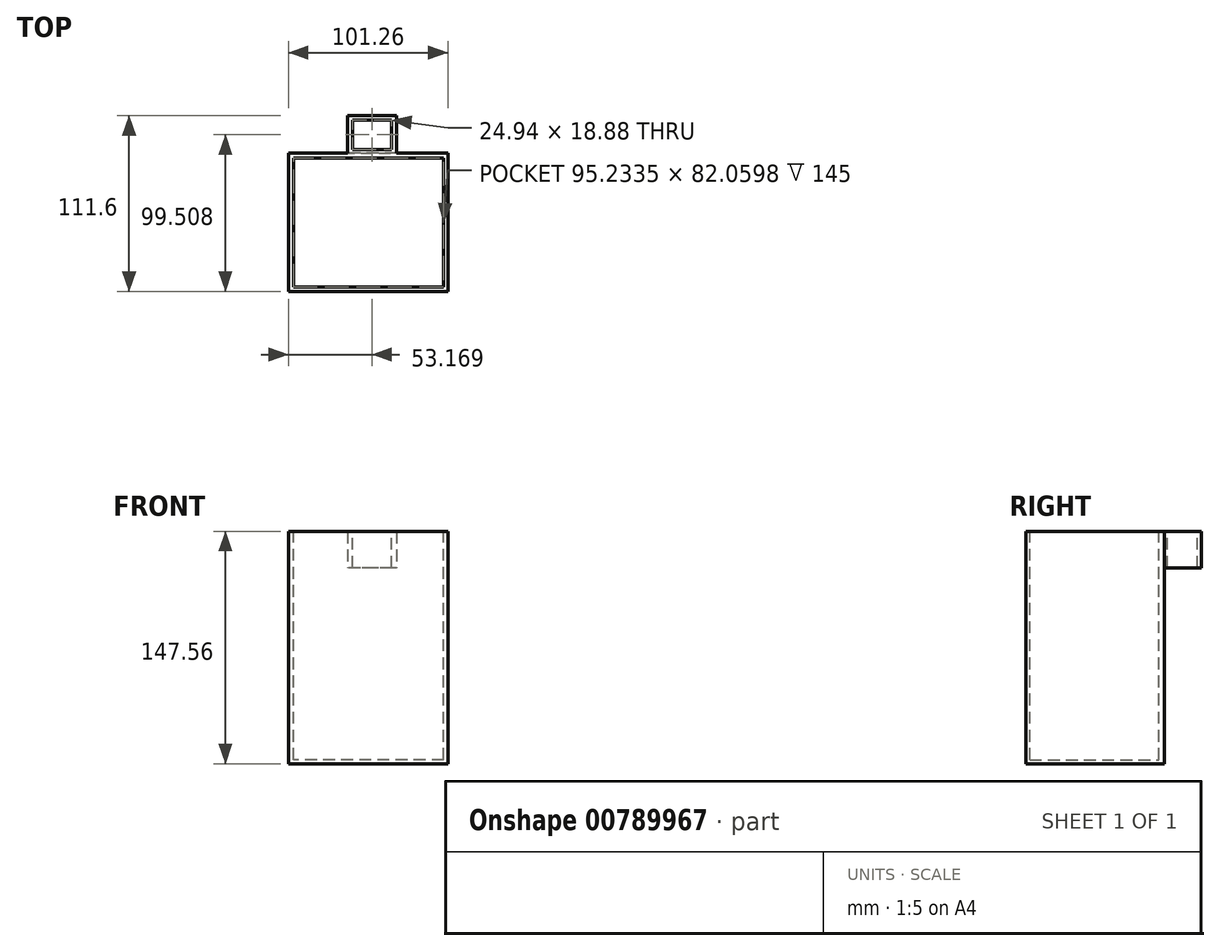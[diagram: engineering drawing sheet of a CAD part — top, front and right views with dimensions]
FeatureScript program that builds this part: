
annotation { "Feature Type Name" : "Feature", "Feature Type Description" : "" }
export const myFeature = defineFeature(function(context is Context, id is Id, definition is map)
    precondition{}
    {
        {
            var Q0;
            Q0=qCreatedBy(makeId("Front.planeOp"),FACE);
            var sketch = newSketch(context, id + "F0", { "sketchPlane" : qUnion([Q0])});
            skLineSegment(sketch, "E0.bottom", {"start": v(-75.3, 74) * mm, "end": v(25.97, 74) * mm});
            skLineSegment(sketch, "E0.top", {"start": v(-75.3, -73.57) * mm, "end": v(25.97, -73.57) * mm});
            skLineSegment(sketch, "E0.left", {"start": v(-75.3, 74) * mm, "end": v(-75.3, -73.57) * mm});
            skLineSegment(sketch, "E0.right", {"start": v(25.97, 74) * mm, "end": v(25.97, -73.57) * mm});
            skSolve(sketch);
        }
        {
            var Q0;
            Q0=makeQuery(id+"F0.imprint","IMPRINT",FACE,{"disambiguationData":[TD([[makeQuery(id+"F0.imprint","IMPRINT",EDGE,{"derivedFrom":sQuery(id+"F0.wireOp",EDGE,"E0.bottom")}),-1.0]])]});
            extrude(context, id + "F1", {"entities" : qUnion([Q0]), "depth" : 88 * mm, "offsetDistance" : 25 * mm});
        }
        {
            var Q0;
            Q0=makeQuery(id+"F1.opExtrude","SWEPT_FACE",FACE,{"disambiguationData":[OSD([sQuery(id+"F0.wireOp",EDGE,"E0.bottom")])]});
            var sketch = newSketch(context, id + "F2", { "sketchPlane" : qUnion([Q0])});
            skLineSegment(sketch, "E1.bottom", {"start": v(23.28, -85.37) * mm, "end": v(-71.96, -85.37) * mm});
            skLineSegment(sketch, "E1.top", {"start": v(23.28, -3.3) * mm, "end": v(-71.96, -3.3) * mm});
            skLineSegment(sketch, "E1.left", {"start": v(23.28, -85.37) * mm, "end": v(23.28, -3.3) * mm});
            skLineSegment(sketch, "E1.right", {"start": v(-71.96, -85.37) * mm, "end": v(-71.96, -3.3) * mm});
            skSolve(sketch);
        }
        {
            var Q0;
            Q0=makeQuery(id+"F2.imprint","IMPRINT",FACE,{"disambiguationData":[TD([[makeQuery(id+"F2.imprint","IMPRINT",EDGE,{"derivedFrom":sQuery(id+"F2.wireOp",EDGE,"E1.bottom")}),-1.0]])]});
            extrude(context, id + "F3", {"entities" : qUnion([Q0]), "operationType" : NewBodyOperationType.REMOVE, "oppositeDirection" : true, "depth" : 145 * mm, "offsetDistance" : 25 * mm});
        }
        {
            var Q0;
            Q0=makeQuery(id+"F1.opExtrude","CAP_FACE",FACE,{"disambiguationData":[OSD([sQuery(id+"F0.wireOp",EDGE,"E0.bottom"),sQuery(id+"F0.wireOp",EDGE,"E0.top"),sQuery(id+"F0.wireOp",EDGE,"E0.left"),sQuery(id+"F0.wireOp",EDGE,"E0.right")])],"isStart":true});
            var sketch = newSketch(context, id + "F4", { "sketchPlane" : qUnion([Q0])});
            skLineSegment(sketch, "E2.bottom", {"start": v(6.55, 74) * mm, "end": v(37.64, 74) * mm});
            skLineSegment(sketch, "E2.top", {"start": v(6.55, 50.94) * mm, "end": v(37.64, 50.94) * mm});
            skLineSegment(sketch, "E2.left", {"start": v(6.55, 74) * mm, "end": v(6.55, 50.94) * mm});
            skLineSegment(sketch, "E2.right", {"start": v(37.64, 74) * mm, "end": v(37.64, 50.94) * mm});
            skSolve(sketch);
        }
        {
            var Q0;
            Q0=makeQuery(id+"F4.imprint","IMPRINT",FACE,{"disambiguationData":[TD([[makeQuery(id+"F4.imprint","IMPRINT",EDGE,{"derivedFrom":sQuery(id+"F4.wireOp",EDGE,"E2.bottom")}),1.0]])]});
            extrude(context, id + "F5", {"entities" : qUnion([Q0]), "operationType" : NewBodyOperationType.ADD, "depth" : 23.6 * mm, "offsetDistance" : 25 * mm});
        }
        {
            var Q0;
            Q0=makeQuery(id+"F5.boolean.opBoolean","MERGE",FACE,{"derivedFrom":[makeQuery(id+"F1.opExtrude","SWEPT_FACE",FACE,{"disambiguationData":[OSD([sQuery(id+"F0.wireOp",EDGE,"E0.bottom")])]}),makeQuery(id+"F5.opExtrude","SWEPT_FACE",FACE,{"disambiguationData":[OSD([sQuery(id+"F4.wireOp",EDGE,"E2.bottom")])]})]});
            var sketch = newSketch(context, id + "F6", { "sketchPlane" : qUnion([Q0])});
            skLineSegment(sketch, "E3.bottom", {"start": v(-34.59, 20.95) * mm, "end": v(-9.65, 20.95) * mm});
            skLineSegment(sketch, "E3.top", {"start": v(-34.59, 2.07) * mm, "end": v(-9.65, 2.07) * mm});
            skLineSegment(sketch, "E3.left", {"start": v(-34.59, 20.95) * mm, "end": v(-34.59, 2.07) * mm});
            skLineSegment(sketch, "E3.right", {"start": v(-9.65, 20.95) * mm, "end": v(-9.65, 2.07) * mm});
            skSolve(sketch);
        }
        {
            var Q0;
            Q0=makeQuery(id+"F6.imprint","IMPRINT",FACE,{"disambiguationData":[TD([[makeQuery(id+"F6.imprint","IMPRINT",EDGE,{"derivedFrom":sQuery(id+"F6.wireOp",EDGE,"E3.bottom")}),-1.0]])]});
            extrude(context, id + "F7", {"entities" : qUnion([Q0]), "operationType" : NewBodyOperationType.REMOVE, "endBound" : BoundingType.UP_TO_NEXT, "oppositeDirection" : true, "depth" : 25 * mm, "offsetDistance" : 25 * mm});
        }
    });
